# Revit family: Gira_015231
name_source: partatom
category: Electrical Fixtures
revit_build: Autodesk Revit 2017 (Build: 20160225_1515(x64)
units: mm (PartAtom-declared; Revit-internal decimal feet)

## family parameters
Always vertical = Yes
Cut with Voids When Loaded = No
Host = Wall
Maintain Annotation Orientation = No
OmniClass Number = 23.80.00.00
OmniClass Title = Electric Power and Lighting
Part Type = Normal
Room Calculation Point = No
Round Connector Dimension = Use Diameter
Shared = No

## types (1)
- Rocker btn NO con. s.sig. in.sp. WD surface-mounted grey
    Assembly arrangement = Basic element with complete housing
    BIM = https://media.live.bim.site und Tasten.rfa
    BIMSITE_PRODUCT_ID = a86cca7390be7d94506371fe1f2a3901298d9343
    Colour = Grey
    Cost = 0 $
    Description = Rock.btn NO con.s.sig.in.sp. WT SM GY Rocker Button 10 AX 250 V~ with inscription space NO contact, 1-pole with sep. signal contact grey Notes : - Can also be connected with illumination.
    GTIN = 4010337152316
    HAN = 015231
    Halogen free = No
    HeinzeBIM = https://www.heinze.de
    Imprint = ohne (*de-DE)
    Label space/information surface YesNo = No
    Manufacturer = Gira
    Material = Sonstige (*de-DE)
    Material quality = Sonstige (*de-DE)
    Method of operation = Rocker
    Model = Single push button
    Nominal voltage [Volt] Number = 250
    Number of modules (module system) = 0
    Number of rockers = 1
    Push button switch = No
    Rated current [Ampere] = 10
    Suitable for degree of protection (IP) = IP66
    Surface protection = Sonstige (*de-DE)
    Transparent = No
    URL = https://www.gira.de
    Washing machine switch = No
    White = White
    With lighting = No
    With mounting plate = No

## geometry (parser evidence)
native form markers: Blend x2, Sweep x6
no freeform markers — native parametric forms only
